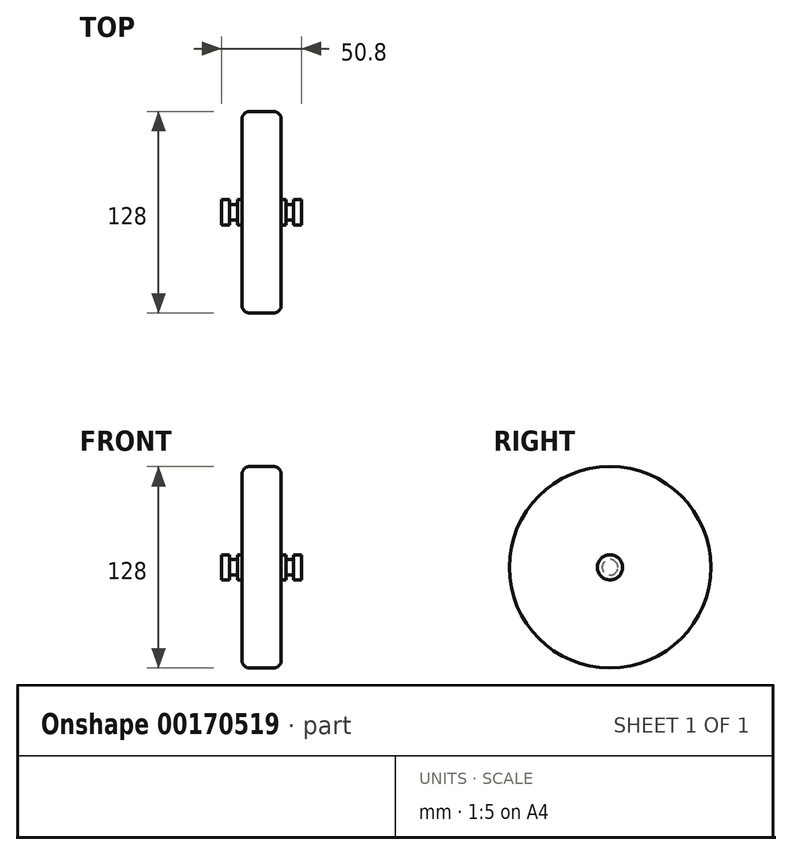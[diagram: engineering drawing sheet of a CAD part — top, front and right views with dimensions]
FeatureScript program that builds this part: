
annotation { "Feature Type Name" : "Feature", "Feature Type Description" : "" }
export const myFeature = defineFeature(function(context is Context, id is Id, definition is map)
    precondition{}
    {
        {
            var Q0;
            Q0=qCreatedBy(makeId("Front.planeOp"),FACE);
            var sketch = newSketch(context, id + "F0", { "sketchPlane" : qUnion([Q0])});
            skLineSegment(sketch, "E0", {"start": v(-87.22, 0) * mm, "end": v(73.7, 0) * mm, "construction": true});
            skLineSegment(sketch, "E1.bottom", {"start": v(-25.4, 8) * mm, "end": v(-20.4, 8) * mm});
            skLineSegment(sketch, "E1.top", {"start": v(-25.4, 0) * mm, "end": v(25.4, 0) * mm});
            skLineSegment(sketch, "E1.left", {"start": v(-25.4, 8) * mm, "end": v(-25.4, 0) * mm});
            skLineSegment(sketch, "E1.right", {"start": v(25.4, 8) * mm, "end": v(25.4, 0) * mm});
            skLineSegment(sketch, "E2.bottom", {"start": v(-7.5, 64) * mm, "end": v(7.5, 64) * mm});
            skLineSegment(sketch, "E2.top", {"start": v(-12.5, 0) * mm, "end": v(12.5, 0) * mm});
            skLineSegment(sketch, "E2.left", {"start": v(-12.5, 59) * mm, "end": v(-12.5, 8) * mm});
            skLineSegment(sketch, "E2.right", {"start": v(12.5, 59) * mm, "end": v(12.5, 8) * mm});
            skLineSegment(sketch, "E3", {"start": v(0, 0) * mm, "end": v(0, 77.8) * mm, "construction": true});
            skPoint(sketch, "E3.endSnap0", {"position": v(0, 64) * mm});
            skPoint(sketch, "E4.visualSharp", {"position": v(-12.5, 64) * mm});
            skArc(sketch, "E4.filletArc", {"start": v(-7.5, 64) * mm, "mid": v(-11.04, 62.54) * mm, "end": v(-12.5, 59) * mm});
            skPoint(sketch, "E5.visualSharp", {"position": v(12.5, 64) * mm});
            skArc(sketch, "E5.filletArc", {"start": v(12.5, 59) * mm, "mid": v(11.04, 62.54) * mm, "end": v(7.5, 64) * mm});
            skLineSegment(sketch, "E6.0", {"start": v(-15.4, 8) * mm, "end": v(-15.4, 5) * mm});
            skLineSegment(sketch, "E7.0", {"start": v(15.4, 8) * mm, "end": v(15.4, 5) * mm});
            skLineSegment(sketch, "E8.0", {"start": v(-20.4, 8) * mm, "end": v(-20.4, 5) * mm});
            skLineSegment(sketch, "E9.0", {"start": v(20.4, 8) * mm, "end": v(20.4, 5) * mm});
            skLineSegment(sketch, "E10.0", {"start": v(-20.4, 5) * mm, "end": v(-15.4, 5) * mm});
            skLineSegment(sketch, "E11.trimOffspring", {"start": v(15.4, 5) * mm, "end": v(20.4, 5) * mm});
            skLineSegment(sketch, "E12.trimOffspring", {"start": v(20.4, 8) * mm, "end": v(25.4, 8) * mm});
            skLineSegment(sketch, "E13.trimOffspring", {"start": v(-15.4, 8) * mm, "end": v(-12.5, 8) * mm});
            skLineSegment(sketch, "E14.trimOffspring", {"start": v(12.5, 8) * mm, "end": v(15.4, 8) * mm});
            skSolve(sketch);
        }
        {
            var Q0;
            Q0=makeQuery(id+"F0.imprint","IMPRINT",FACE,{"disambiguationData":[TD([[makeQuery(id+"F0.imprint","IMPRINT",EDGE,{"derivedFrom":sQuery(id+"F0.wireOp",EDGE,"E1.bottom")}),-1.0]])]});
            var Q1;
            Q1=sQuery(id+"F0.wireOp",EDGE,"E0");
            revolve(context, id + "F1", {"entities" : qUnion([Q0]), "axis" : qUnion([Q1]), "revolveType" : RevolveType.FULL});
        }
    });
